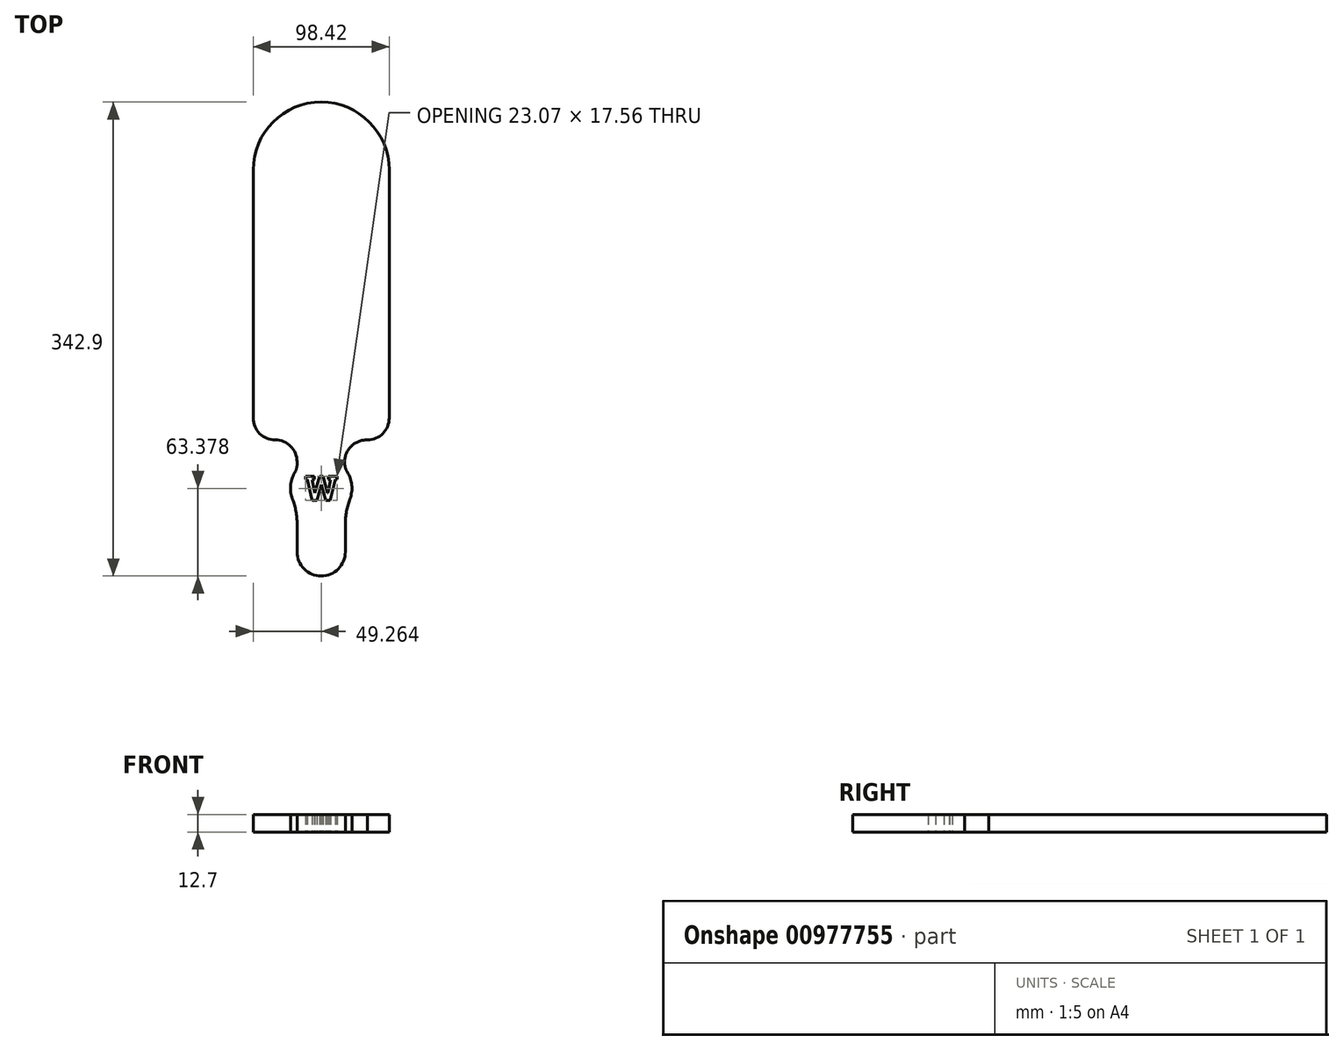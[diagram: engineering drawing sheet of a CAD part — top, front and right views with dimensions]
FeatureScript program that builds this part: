
annotation { "Feature Type Name" : "Feature", "Feature Type Description" : "" }
export const myFeature = defineFeature(function(context is Context, id is Id, definition is map)
    precondition{}
    {
        {
            var Q0;
            Q0=qCreatedBy(makeId("Top.planeOp"),FACE);
            var sketch = newSketch(context, id + "F0", { "sketchPlane" : qUnion([Q0])});
            skLineSegment(sketch, "E0.top", {"start": v(44.45, 0) * mm, "end": v(44.45, 0) * mm});
            skLineSegment(sketch, "E0.left", {"start": v(0, 298.45) * mm, "end": v(0, 117.48) * mm});
            skLineSegment(sketch, "E0.right", {"start": v(88.9, 298.45) * mm, "end": v(88.9, 117.48) * mm});
            skLineSegment(sketch, "E1.top", {"start": v(15.88, 101.6) * mm, "end": v(15.88, 101.6) * mm});
            skLineSegment(sketch, "E1.right", {"start": v(31.75, 12.7) * mm, "end": v(31.75, 85.73) * mm});
            skLineSegment(sketch, "E2.top", {"start": v(73.02, 101.6) * mm, "end": v(73.02, 101.6) * mm});
            skLineSegment(sketch, "E2.right", {"start": v(57.15, 12.7) * mm, "end": v(57.15, 85.73) * mm});
            skPoint(sketch, "E2.bottom.start.orphan", {"position": v(88.9, 0) * mm});
            skPoint(sketch, "E3.visualSharp", {"position": v(0, 101.6) * mm});
            skArc(sketch, "E3.filletArc", {"start": v(0, 117.48) * mm, "mid": v(4.65, 106.25) * mm, "end": v(15.88, 101.6) * mm});
            skPoint(sketch, "E4.visualSharp", {"position": v(88.9, 101.6) * mm});
            skArc(sketch, "E4.filletArc", {"start": v(73.02, 101.6) * mm, "mid": v(84.25, 106.25) * mm, "end": v(88.9, 117.48) * mm});
            skPoint(sketch, "E5.visualSharp", {"position": v(57.15, 101.6) * mm});
            skArc(sketch, "E5.filletArc", {"start": v(73.02, 101.6) * mm, "mid": v(61.8, 96.95) * mm, "end": v(57.15, 85.73) * mm});
            skPoint(sketch, "E6.visualSharp", {"position": v(31.75, 101.6) * mm});
            skArc(sketch, "E6.filletArc", {"start": v(31.75, 85.73) * mm, "mid": v(27.1, 96.95) * mm, "end": v(15.88, 101.6) * mm});
            skPoint(sketch, "E7.visualSharp", {"position": v(31.75, 0) * mm});
            skArc(sketch, "E7.filletArc", {"start": v(31.75, 12.7) * mm, "mid": v(35.47, 3.72) * mm, "end": v(44.45, 0) * mm});
            skPoint(sketch, "E8.visualSharp", {"position": v(57.15, 0) * mm});
            skArc(sketch, "E8.filletArc", {"start": v(44.45, 0) * mm, "mid": v(53.43, 3.72) * mm, "end": v(57.15, 12.7) * mm});
            skFitSpline(sketch, "E9", {"points": [v(31.75, 85.73) * mm, v(25.4, 50.8) * mm, v(31.75, 12.7) * mm], "startDerivative": vector(0, -58.38) * mm, "endDerivative": vector(0, -74.62) * mm});
            skFitSpline(sketch, "E10", {"points": [v(57.15, 85.73) * mm, v(63.5, 50.8) * mm, v(57.15, 12.7) * mm], "startDerivative": vector(0, -58.38) * mm, "endDerivative": vector(0, -74.62) * mm});
            skArc(sketch, "E11", {"start": v(88.9, 298.45) * mm, "mid": v(44.45, 342.9) * mm, "end": v(0, 298.45) * mm});
            skLineSegment(sketch, "E12.bottom", {"start": v(15.87, 317.5) * mm, "end": v(73.02, 317.5) * mm, "construction": true});
            skLineSegment(sketch, "E12.top", {"start": v(15.88, 117.48) * mm, "end": v(73.02, 117.48) * mm, "construction": true});
            skLineSegment(sketch, "E12.left", {"start": v(15.87, 317.5) * mm, "end": v(15.88, 117.48) * mm, "construction": true});
            skLineSegment(sketch, "E12.right", {"start": v(73.02, 317.5) * mm, "end": v(73.02, 117.48) * mm, "construction": true});
            skPoint(sketch, "E13.1.0.0", {"position": v(187.32, 0) * mm});
            skPoint(sketch, "E13.1.0.1", {"position": v(155.58, 101.6) * mm});
            skArc(sketch, "E13.1.0.2", {"start": v(187.33, 298.45) * mm, "mid": v(142.88, 342.9) * mm, "end": v(98.42, 298.45) * mm});
            skPoint(sketch, "E13.1.0.3", {"position": v(130.18, 0) * mm});
            skLineSegment(sketch, "E13.1.0.4", {"start": v(130.18, 12.7) * mm, "end": v(130.18, 85.73) * mm});
            skLineSegment(sketch, "E13.1.0.5", {"start": v(171.45, 317.5) * mm, "end": v(171.45, 117.47) * mm, "construction": true});
            skPoint(sketch, "E13.1.0.6", {"position": v(187.32, 101.6) * mm});
            skLineSegment(sketch, "E13.1.0.7", {"start": v(114.3, 317.5) * mm, "end": v(114.3, 117.47) * mm, "construction": true});
            skLineSegment(sketch, "E13.1.0.8", {"start": v(98.43, 298.45) * mm, "end": v(98.43, 117.47) * mm});
            skPoint(sketch, "E13.1.0.9", {"position": v(130.17, 101.6) * mm});
            skPoint(sketch, "E13.1.0.10", {"position": v(155.58, 0) * mm});
            skLineSegment(sketch, "E13.1.0.11", {"start": v(114.3, 317.5) * mm, "end": v(171.45, 317.5) * mm, "construction": true});
            skPoint(sketch, "E13.1.0.12", {"position": v(98.43, 101.6) * mm});
            skLineSegment(sketch, "E13.1.0.13", {"start": v(187.32, 298.45) * mm, "end": v(187.32, 117.47) * mm});
            skLineSegment(sketch, "E13.1.0.14", {"start": v(155.58, 12.7) * mm, "end": v(155.58, 85.73) * mm});
            skLineSegment(sketch, "E13.1.0.15", {"start": v(114.3, 117.47) * mm, "end": v(171.45, 117.47) * mm, "construction": true});
            skArc(sketch, "E13.1.0.16", {"start": v(98.43, 117.47) * mm, "mid": v(103.07, 106.25) * mm, "end": v(114.3, 101.6) * mm});
            skArc(sketch, "E13.1.0.17", {"start": v(171.45, 101.6) * mm, "mid": v(160.22, 96.95) * mm, "end": v(155.57, 85.73) * mm});
            skArc(sketch, "E13.1.0.18", {"start": v(130.18, 85.73) * mm, "mid": v(125.53, 96.95) * mm, "end": v(114.3, 101.6) * mm});
            skArc(sketch, "E13.1.0.19", {"start": v(142.88, 0) * mm, "mid": v(151.86, 3.72) * mm, "end": v(155.57, 12.7) * mm});
            skArc(sketch, "E13.1.0.20", {"start": v(171.45, 101.6) * mm, "mid": v(182.68, 106.25) * mm, "end": v(187.32, 117.47) * mm});
            skArc(sketch, "E13.1.0.21", {"start": v(130.17, 12.7) * mm, "mid": v(133.9, 3.72) * mm, "end": v(142.87, 0) * mm});
            skPoint(sketch, "E13.2.0.0", {"position": v(285.75, 0) * mm});
            skPoint(sketch, "E13.2.0.1", {"position": v(254, 101.6) * mm});
            skArc(sketch, "E13.2.0.2", {"start": v(285.75, 298.45) * mm, "mid": v(241.3, 342.9) * mm, "end": v(196.85, 298.45) * mm});
            skPoint(sketch, "E13.2.0.3", {"position": v(228.6, 0) * mm});
            skLineSegment(sketch, "E13.2.0.4", {"start": v(228.6, 12.7) * mm, "end": v(228.6, 85.73) * mm});
            skLineSegment(sketch, "E13.2.0.5", {"start": v(269.87, 317.5) * mm, "end": v(269.87, 117.47) * mm, "construction": true});
            skPoint(sketch, "E13.2.0.6", {"position": v(285.75, 101.6) * mm});
            skLineSegment(sketch, "E13.2.0.7", {"start": v(212.73, 317.5) * mm, "end": v(212.73, 117.47) * mm, "construction": true});
            skLineSegment(sketch, "E13.2.0.8", {"start": v(196.85, 298.45) * mm, "end": v(196.85, 117.47) * mm});
            skPoint(sketch, "E13.2.0.9", {"position": v(228.6, 101.6) * mm});
            skPoint(sketch, "E13.2.0.10", {"position": v(254, 0) * mm});
            skLineSegment(sketch, "E13.2.0.11", {"start": v(212.72, 317.5) * mm, "end": v(269.87, 317.5) * mm, "construction": true});
            skPoint(sketch, "E13.2.0.12", {"position": v(196.85, 101.6) * mm});
            skLineSegment(sketch, "E13.2.0.13", {"start": v(285.75, 298.45) * mm, "end": v(285.75, 117.47) * mm});
            skLineSegment(sketch, "E13.2.0.14", {"start": v(254, 12.7) * mm, "end": v(254, 85.73) * mm});
            skLineSegment(sketch, "E13.2.0.15", {"start": v(212.73, 117.47) * mm, "end": v(269.87, 117.47) * mm, "construction": true});
            skArc(sketch, "E13.2.0.16", {"start": v(196.85, 117.47) * mm, "mid": v(201.5, 106.25) * mm, "end": v(212.73, 101.6) * mm});
            skArc(sketch, "E13.2.0.17", {"start": v(269.88, 101.6) * mm, "mid": v(258.65, 96.95) * mm, "end": v(254, 85.73) * mm});
            skArc(sketch, "E13.2.0.18", {"start": v(228.6, 85.73) * mm, "mid": v(223.95, 96.95) * mm, "end": v(212.73, 101.6) * mm});
            skArc(sketch, "E13.2.0.19", {"start": v(241.3, 0) * mm, "mid": v(250.28, 3.72) * mm, "end": v(254, 12.7) * mm});
            skArc(sketch, "E13.2.0.20", {"start": v(269.87, 101.6) * mm, "mid": v(281.1, 106.25) * mm, "end": v(285.75, 117.47) * mm});
            skArc(sketch, "E13.2.0.21", {"start": v(228.6, 12.7) * mm, "mid": v(232.32, 3.72) * mm, "end": v(241.3, 0) * mm});
            skPoint(sketch, "E13.3.0.0", {"position": v(384.17, 0) * mm});
            skPoint(sketch, "E13.3.0.1", {"position": v(352.43, 101.6) * mm});
            skArc(sketch, "E13.3.0.2", {"start": v(384.18, 298.45) * mm, "mid": v(339.73, 342.9) * mm, "end": v(295.28, 298.45) * mm});
            skPoint(sketch, "E13.3.0.3", {"position": v(327.03, 0) * mm});
            skLineSegment(sketch, "E13.3.0.4", {"start": v(327.03, 12.7) * mm, "end": v(327.03, 85.73) * mm});
            skLineSegment(sketch, "E13.3.0.5", {"start": v(368.3, 317.5) * mm, "end": v(368.3, 117.47) * mm, "construction": true});
            skPoint(sketch, "E13.3.0.6", {"position": v(384.17, 101.6) * mm});
            skLineSegment(sketch, "E13.3.0.7", {"start": v(311.15, 317.5) * mm, "end": v(311.15, 117.47) * mm, "construction": true});
            skLineSegment(sketch, "E13.3.0.8", {"start": v(295.28, 298.45) * mm, "end": v(295.28, 117.47) * mm});
            skPoint(sketch, "E13.3.0.9", {"position": v(327.03, 101.6) * mm});
            skPoint(sketch, "E13.3.0.10", {"position": v(352.43, 0) * mm});
            skLineSegment(sketch, "E13.3.0.11", {"start": v(311.15, 317.5) * mm, "end": v(368.3, 317.5) * mm, "construction": true});
            skPoint(sketch, "E13.3.0.12", {"position": v(295.28, 101.6) * mm});
            skLineSegment(sketch, "E13.3.0.13", {"start": v(384.17, 298.45) * mm, "end": v(384.17, 117.47) * mm});
            skLineSegment(sketch, "E13.3.0.14", {"start": v(352.43, 12.7) * mm, "end": v(352.43, 85.73) * mm});
            skLineSegment(sketch, "E13.3.0.15", {"start": v(311.15, 117.47) * mm, "end": v(368.3, 117.47) * mm, "construction": true});
            skArc(sketch, "E13.3.0.16", {"start": v(295.28, 117.47) * mm, "mid": v(299.92, 106.25) * mm, "end": v(311.15, 101.6) * mm});
            skArc(sketch, "E13.3.0.17", {"start": v(368.3, 101.6) * mm, "mid": v(357.07, 96.95) * mm, "end": v(352.43, 85.73) * mm});
            skArc(sketch, "E13.3.0.18", {"start": v(327.03, 85.73) * mm, "mid": v(322.38, 96.95) * mm, "end": v(311.15, 101.6) * mm});
            skArc(sketch, "E13.3.0.19", {"start": v(339.73, 0) * mm, "mid": v(348.7, 3.72) * mm, "end": v(352.43, 12.7) * mm});
            skArc(sketch, "E13.3.0.20", {"start": v(368.3, 101.6) * mm, "mid": v(379.53, 106.25) * mm, "end": v(384.17, 117.47) * mm});
            skArc(sketch, "E13.3.0.21", {"start": v(327.02, 12.7) * mm, "mid": v(330.74, 3.72) * mm, "end": v(339.72, 0) * mm});
            skPoint(sketch, "E13.4.0.0", {"position": v(482.6, 0) * mm});
            skPoint(sketch, "E13.4.0.1", {"position": v(450.85, 101.6) * mm});
            skArc(sketch, "E13.4.0.2", {"start": v(482.6, 298.45) * mm, "mid": v(438.15, 342.9) * mm, "end": v(393.7, 298.45) * mm});
            skPoint(sketch, "E13.4.0.3", {"position": v(425.45, 0) * mm});
            skLineSegment(sketch, "E13.4.0.4", {"start": v(425.45, 12.7) * mm, "end": v(425.45, 85.73) * mm});
            skLineSegment(sketch, "E13.4.0.5", {"start": v(466.72, 317.5) * mm, "end": v(466.72, 117.47) * mm, "construction": true});
            skPoint(sketch, "E13.4.0.6", {"position": v(482.6, 101.6) * mm});
            skLineSegment(sketch, "E13.4.0.7", {"start": v(409.58, 317.5) * mm, "end": v(409.58, 117.47) * mm, "construction": true});
            skLineSegment(sketch, "E13.4.0.8", {"start": v(393.7, 298.45) * mm, "end": v(393.7, 117.47) * mm});
            skPoint(sketch, "E13.4.0.9", {"position": v(425.45, 101.6) * mm});
            skPoint(sketch, "E13.4.0.10", {"position": v(450.85, 0) * mm});
            skLineSegment(sketch, "E13.4.0.11", {"start": v(409.58, 317.5) * mm, "end": v(466.72, 317.5) * mm, "construction": true});
            skPoint(sketch, "E13.4.0.12", {"position": v(393.7, 101.6) * mm});
            skLineSegment(sketch, "E13.4.0.13", {"start": v(482.6, 298.45) * mm, "end": v(482.6, 117.47) * mm});
            skLineSegment(sketch, "E13.4.0.14", {"start": v(450.85, 12.7) * mm, "end": v(450.85, 85.73) * mm});
            skLineSegment(sketch, "E13.4.0.15", {"start": v(409.58, 117.47) * mm, "end": v(466.72, 117.47) * mm, "construction": true});
            skArc(sketch, "E13.4.0.16", {"start": v(393.7, 117.47) * mm, "mid": v(398.35, 106.25) * mm, "end": v(409.58, 101.6) * mm});
            skArc(sketch, "E13.4.0.17", {"start": v(466.73, 101.6) * mm, "mid": v(455.5, 96.95) * mm, "end": v(450.85, 85.73) * mm});
            skArc(sketch, "E13.4.0.18", {"start": v(425.45, 85.73) * mm, "mid": v(420.8, 96.95) * mm, "end": v(409.58, 101.6) * mm});
            skArc(sketch, "E13.4.0.19", {"start": v(438.15, 0) * mm, "mid": v(447.13, 3.72) * mm, "end": v(450.85, 12.7) * mm});
            skArc(sketch, "E13.4.0.20", {"start": v(466.72, 101.6) * mm, "mid": v(477.95, 106.25) * mm, "end": v(482.6, 117.47) * mm});
            skArc(sketch, "E13.4.0.21", {"start": v(425.45, 12.7) * mm, "mid": v(429.17, 3.72) * mm, "end": v(438.15, 0) * mm});
            skPoint(sketch, "E13.5.0.0", {"position": v(581.02, 0) * mm});
            skPoint(sketch, "E13.5.0.1", {"position": v(549.28, 101.6) * mm});
            skArc(sketch, "E13.5.0.2", {"start": v(581.02, 298.45) * mm, "mid": v(536.58, 342.9) * mm, "end": v(492.13, 298.45) * mm});
            skPoint(sketch, "E13.5.0.3", {"position": v(523.88, 0) * mm});
            skLineSegment(sketch, "E13.5.0.4", {"start": v(523.88, 12.7) * mm, "end": v(523.88, 85.73) * mm});
            skLineSegment(sketch, "E13.5.0.5", {"start": v(565.15, 317.5) * mm, "end": v(565.15, 117.47) * mm, "construction": true});
            skPoint(sketch, "E13.5.0.6", {"position": v(581.02, 101.6) * mm});
            skLineSegment(sketch, "E13.5.0.7", {"start": v(508, 317.5) * mm, "end": v(508, 117.47) * mm, "construction": true});
            skLineSegment(sketch, "E13.5.0.8", {"start": v(492.13, 298.45) * mm, "end": v(492.13, 117.47) * mm});
            skPoint(sketch, "E13.5.0.9", {"position": v(523.88, 101.6) * mm});
            skPoint(sketch, "E13.5.0.10", {"position": v(549.28, 0) * mm});
            skLineSegment(sketch, "E13.5.0.11", {"start": v(508, 317.5) * mm, "end": v(565.15, 317.5) * mm, "construction": true});
            skPoint(sketch, "E13.5.0.12", {"position": v(492.13, 101.6) * mm});
            skLineSegment(sketch, "E13.5.0.13", {"start": v(581.02, 298.45) * mm, "end": v(581.02, 117.47) * mm});
            skLineSegment(sketch, "E13.5.0.14", {"start": v(549.27, 12.7) * mm, "end": v(549.27, 85.73) * mm});
            skLineSegment(sketch, "E13.5.0.15", {"start": v(508, 117.47) * mm, "end": v(565.15, 117.47) * mm, "construction": true});
            skArc(sketch, "E13.5.0.16", {"start": v(492.13, 117.47) * mm, "mid": v(496.77, 106.25) * mm, "end": v(508, 101.6) * mm});
            skArc(sketch, "E13.5.0.17", {"start": v(565.15, 101.6) * mm, "mid": v(553.92, 96.95) * mm, "end": v(549.28, 85.73) * mm});
            skArc(sketch, "E13.5.0.18", {"start": v(523.88, 85.73) * mm, "mid": v(519.23, 96.95) * mm, "end": v(508, 101.6) * mm});
            skArc(sketch, "E13.5.0.19", {"start": v(536.58, 0) * mm, "mid": v(545.56, 3.72) * mm, "end": v(549.28, 12.7) * mm});
            skArc(sketch, "E13.5.0.20", {"start": v(565.15, 101.6) * mm, "mid": v(576.38, 106.25) * mm, "end": v(581.02, 117.47) * mm});
            skArc(sketch, "E13.5.0.21", {"start": v(523.87, 12.7) * mm, "mid": v(527.6, 3.72) * mm, "end": v(536.57, 0) * mm});
            skPoint(sketch, "E13.6.0.0", {"position": v(679.45, 0) * mm});
            skPoint(sketch, "E13.6.0.1", {"position": v(647.7, 101.6) * mm});
            skArc(sketch, "E13.6.0.2", {"start": v(679.45, 298.45) * mm, "mid": v(635, 342.9) * mm, "end": v(590.55, 298.45) * mm});
            skPoint(sketch, "E13.6.0.3", {"position": v(622.3, 0) * mm});
            skLineSegment(sketch, "E13.6.0.4", {"start": v(622.3, 12.7) * mm, "end": v(622.3, 85.73) * mm});
            skLineSegment(sketch, "E13.6.0.5", {"start": v(663.57, 317.5) * mm, "end": v(663.57, 117.47) * mm, "construction": true});
            skPoint(sketch, "E13.6.0.6", {"position": v(679.45, 101.6) * mm});
            skLineSegment(sketch, "E13.6.0.7", {"start": v(606.43, 317.5) * mm, "end": v(606.43, 117.47) * mm, "construction": true});
            skLineSegment(sketch, "E13.6.0.8", {"start": v(590.55, 298.45) * mm, "end": v(590.55, 117.47) * mm});
            skPoint(sketch, "E13.6.0.9", {"position": v(622.3, 101.6) * mm});
            skPoint(sketch, "E13.6.0.10", {"position": v(647.7, 0) * mm});
            skLineSegment(sketch, "E13.6.0.11", {"start": v(606.43, 317.5) * mm, "end": v(663.57, 317.5) * mm, "construction": true});
            skPoint(sketch, "E13.6.0.12", {"position": v(590.55, 101.6) * mm});
            skLineSegment(sketch, "E13.6.0.13", {"start": v(679.45, 298.45) * mm, "end": v(679.45, 117.47) * mm});
            skLineSegment(sketch, "E13.6.0.14", {"start": v(647.7, 12.7) * mm, "end": v(647.7, 85.73) * mm});
            skLineSegment(sketch, "E13.6.0.15", {"start": v(606.43, 117.47) * mm, "end": v(663.57, 117.47) * mm, "construction": true});
            skArc(sketch, "E13.6.0.16", {"start": v(590.55, 117.47) * mm, "mid": v(595.2, 106.25) * mm, "end": v(606.43, 101.6) * mm});
            skArc(sketch, "E13.6.0.17", {"start": v(663.58, 101.6) * mm, "mid": v(652.35, 96.95) * mm, "end": v(647.7, 85.73) * mm});
            skArc(sketch, "E13.6.0.18", {"start": v(622.3, 85.73) * mm, "mid": v(617.65, 96.95) * mm, "end": v(606.43, 101.6) * mm});
            skArc(sketch, "E13.6.0.19", {"start": v(635, 0) * mm, "mid": v(643.98, 3.72) * mm, "end": v(647.7, 12.7) * mm});
            skArc(sketch, "E13.6.0.20", {"start": v(663.57, 101.6) * mm, "mid": v(674.8, 106.25) * mm, "end": v(679.45, 117.47) * mm});
            skArc(sketch, "E13.6.0.21", {"start": v(622.3, 12.7) * mm, "mid": v(626.02, 3.72) * mm, "end": v(635, 0) * mm});
            skPoint(sketch, "E13.7.0.0", {"position": v(777.87, 0) * mm});
            skPoint(sketch, "E13.7.0.1", {"position": v(746.13, 101.6) * mm});
            skArc(sketch, "E13.7.0.2", {"start": v(777.88, 298.45) * mm, "mid": v(733.43, 342.9) * mm, "end": v(688.98, 298.45) * mm});
            skPoint(sketch, "E13.7.0.3", {"position": v(720.73, 0) * mm});
            skLineSegment(sketch, "E13.7.0.4", {"start": v(720.73, 12.7) * mm, "end": v(720.73, 85.73) * mm});
            skLineSegment(sketch, "E13.7.0.5", {"start": v(762, 317.5) * mm, "end": v(762, 117.47) * mm, "construction": true});
            skPoint(sketch, "E13.7.0.6", {"position": v(777.87, 101.6) * mm});
            skLineSegment(sketch, "E13.7.0.7", {"start": v(704.85, 317.5) * mm, "end": v(704.85, 117.47) * mm, "construction": true});
            skLineSegment(sketch, "E13.7.0.8", {"start": v(688.98, 298.45) * mm, "end": v(688.98, 117.47) * mm});
            skPoint(sketch, "E13.7.0.9", {"position": v(720.73, 101.6) * mm});
            skPoint(sketch, "E13.7.0.10", {"position": v(746.13, 0) * mm});
            skLineSegment(sketch, "E13.7.0.11", {"start": v(704.85, 317.5) * mm, "end": v(762, 317.5) * mm, "construction": true});
            skPoint(sketch, "E13.7.0.12", {"position": v(688.98, 101.6) * mm});
            skLineSegment(sketch, "E13.7.0.13", {"start": v(777.87, 298.45) * mm, "end": v(777.87, 117.47) * mm});
            skLineSegment(sketch, "E13.7.0.14", {"start": v(746.13, 12.7) * mm, "end": v(746.13, 85.73) * mm});
            skLineSegment(sketch, "E13.7.0.15", {"start": v(704.85, 117.47) * mm, "end": v(762, 117.47) * mm, "construction": true});
            skArc(sketch, "E13.7.0.16", {"start": v(688.98, 117.47) * mm, "mid": v(693.62, 106.25) * mm, "end": v(704.85, 101.6) * mm});
            skArc(sketch, "E13.7.0.17", {"start": v(762, 101.6) * mm, "mid": v(750.77, 96.95) * mm, "end": v(746.13, 85.73) * mm});
            skArc(sketch, "E13.7.0.18", {"start": v(720.73, 85.73) * mm, "mid": v(716.08, 96.95) * mm, "end": v(704.85, 101.6) * mm});
            skArc(sketch, "E13.7.0.19", {"start": v(733.43, 0) * mm, "mid": v(742.4, 3.72) * mm, "end": v(746.13, 12.7) * mm});
            skArc(sketch, "E13.7.0.20", {"start": v(762, 101.6) * mm, "mid": v(773.23, 106.25) * mm, "end": v(777.87, 117.47) * mm});
            skArc(sketch, "E13.7.0.21", {"start": v(720.72, 12.7) * mm, "mid": v(724.44, 3.72) * mm, "end": v(733.42, 0) * mm});
            skPoint(sketch, "E13.8.0.0", {"position": v(876.3, 0) * mm});
            skPoint(sketch, "E13.8.0.1", {"position": v(844.55, 101.6) * mm});
            skArc(sketch, "E13.8.0.2", {"start": v(876.3, 298.45) * mm, "mid": v(831.85, 342.9) * mm, "end": v(787.4, 298.45) * mm});
            skPoint(sketch, "E13.8.0.3", {"position": v(819.15, 0) * mm});
            skLineSegment(sketch, "E13.8.0.4", {"start": v(819.15, 12.7) * mm, "end": v(819.15, 85.73) * mm});
            skLineSegment(sketch, "E13.8.0.5", {"start": v(860.42, 317.5) * mm, "end": v(860.42, 117.47) * mm, "construction": true});
            skPoint(sketch, "E13.8.0.6", {"position": v(876.3, 101.6) * mm});
            skLineSegment(sketch, "E13.8.0.7", {"start": v(803.28, 317.5) * mm, "end": v(803.28, 117.47) * mm, "construction": true});
            skLineSegment(sketch, "E13.8.0.8", {"start": v(787.4, 298.45) * mm, "end": v(787.4, 117.47) * mm});
            skPoint(sketch, "E13.8.0.9", {"position": v(819.15, 101.6) * mm});
            skPoint(sketch, "E13.8.0.10", {"position": v(844.55, 0) * mm});
            skLineSegment(sketch, "E13.8.0.11", {"start": v(803.28, 317.5) * mm, "end": v(860.42, 317.5) * mm, "construction": true});
            skPoint(sketch, "E13.8.0.12", {"position": v(787.4, 101.6) * mm});
            skLineSegment(sketch, "E13.8.0.13", {"start": v(876.3, 298.45) * mm, "end": v(876.3, 117.47) * mm});
            skLineSegment(sketch, "E13.8.0.14", {"start": v(844.55, 12.7) * mm, "end": v(844.55, 85.73) * mm});
            skLineSegment(sketch, "E13.8.0.15", {"start": v(803.28, 117.47) * mm, "end": v(860.42, 117.47) * mm, "construction": true});
            skArc(sketch, "E13.8.0.16", {"start": v(787.4, 117.47) * mm, "mid": v(792.05, 106.25) * mm, "end": v(803.28, 101.6) * mm});
            skArc(sketch, "E13.8.0.17", {"start": v(860.43, 101.6) * mm, "mid": v(849.2, 96.95) * mm, "end": v(844.55, 85.73) * mm});
            skArc(sketch, "E13.8.0.18", {"start": v(819.15, 85.73) * mm, "mid": v(814.5, 96.95) * mm, "end": v(803.28, 101.6) * mm});
            skArc(sketch, "E13.8.0.19", {"start": v(831.85, 0) * mm, "mid": v(840.83, 3.72) * mm, "end": v(844.55, 12.7) * mm});
            skArc(sketch, "E13.8.0.20", {"start": v(860.42, 101.6) * mm, "mid": v(871.65, 106.25) * mm, "end": v(876.3, 117.47) * mm});
            skArc(sketch, "E13.8.0.21", {"start": v(819.15, 12.7) * mm, "mid": v(822.87, 3.72) * mm, "end": v(831.85, 0) * mm});
            skPoint(sketch, "E13.9.0.0", {"position": v(974.72, 0) * mm});
            skPoint(sketch, "E13.9.0.1", {"position": v(942.98, 101.6) * mm});
            skArc(sketch, "E13.9.0.2", {"start": v(974.73, 298.45) * mm, "mid": v(930.28, 342.9) * mm, "end": v(885.83, 298.45) * mm});
            skPoint(sketch, "E13.9.0.3", {"position": v(917.58, 0) * mm});
            skLineSegment(sketch, "E13.9.0.4", {"start": v(917.58, 12.7) * mm, "end": v(917.58, 85.73) * mm});
            skLineSegment(sketch, "E13.9.0.5", {"start": v(958.85, 317.5) * mm, "end": v(958.85, 117.47) * mm, "construction": true});
            skPoint(sketch, "E13.9.0.6", {"position": v(974.72, 101.6) * mm});
            skLineSegment(sketch, "E13.9.0.7", {"start": v(901.7, 317.5) * mm, "end": v(901.7, 117.47) * mm, "construction": true});
            skLineSegment(sketch, "E13.9.0.8", {"start": v(885.83, 298.45) * mm, "end": v(885.83, 117.47) * mm});
            skPoint(sketch, "E13.9.0.9", {"position": v(917.58, 101.6) * mm});
            skPoint(sketch, "E13.9.0.10", {"position": v(942.98, 0) * mm});
            skLineSegment(sketch, "E13.9.0.11", {"start": v(901.7, 317.5) * mm, "end": v(958.85, 317.5) * mm, "construction": true});
            skPoint(sketch, "E13.9.0.12", {"position": v(885.83, 101.6) * mm});
            skLineSegment(sketch, "E13.9.0.13", {"start": v(974.72, 298.45) * mm, "end": v(974.72, 117.47) * mm});
            skLineSegment(sketch, "E13.9.0.14", {"start": v(942.98, 12.7) * mm, "end": v(942.98, 85.73) * mm});
            skLineSegment(sketch, "E13.9.0.15", {"start": v(901.7, 117.47) * mm, "end": v(958.85, 117.47) * mm, "construction": true});
            skArc(sketch, "E13.9.0.16", {"start": v(885.83, 117.47) * mm, "mid": v(890.47, 106.25) * mm, "end": v(901.7, 101.6) * mm});
            skArc(sketch, "E13.9.0.17", {"start": v(958.85, 101.6) * mm, "mid": v(947.62, 96.95) * mm, "end": v(942.98, 85.73) * mm});
            skArc(sketch, "E13.9.0.18", {"start": v(917.58, 85.73) * mm, "mid": v(912.93, 96.95) * mm, "end": v(901.7, 101.6) * mm});
            skArc(sketch, "E13.9.0.19", {"start": v(930.28, 0) * mm, "mid": v(939.26, 3.72) * mm, "end": v(942.98, 12.7) * mm});
            skArc(sketch, "E13.9.0.20", {"start": v(958.85, 101.6) * mm, "mid": v(970.08, 106.25) * mm, "end": v(974.72, 117.47) * mm});
            skArc(sketch, "E13.9.0.21", {"start": v(917.57, 12.7) * mm, "mid": v(921.3, 3.72) * mm, "end": v(930.27, 0) * mm});
            skPoint(sketch, "E13.10.0.0", {"position": v(1073.15, 0) * mm});
            skPoint(sketch, "E13.10.0.1", {"position": v(1041.4, 101.6) * mm});
            skArc(sketch, "E13.10.0.2", {"start": v(1073.15, 298.45) * mm, "mid": v(1028.7, 342.9) * mm, "end": v(984.25, 298.45) * mm});
            skPoint(sketch, "E13.10.0.3", {"position": v(1016, 0) * mm});
            skLineSegment(sketch, "E13.10.0.4", {"start": v(1016, 12.7) * mm, "end": v(1016, 85.73) * mm});
            skLineSegment(sketch, "E13.10.0.5", {"start": v(1057.27, 317.5) * mm, "end": v(1057.27, 117.47) * mm, "construction": true});
            skPoint(sketch, "E13.10.0.6", {"position": v(1073.15, 101.6) * mm});
            skLineSegment(sketch, "E13.10.0.7", {"start": v(1000.13, 317.5) * mm, "end": v(1000.13, 117.47) * mm, "construction": true});
            skLineSegment(sketch, "E13.10.0.8", {"start": v(984.25, 298.45) * mm, "end": v(984.25, 117.47) * mm});
            skPoint(sketch, "E13.10.0.9", {"position": v(1016, 101.6) * mm});
            skPoint(sketch, "E13.10.0.10", {"position": v(1041.4, 0) * mm});
            skLineSegment(sketch, "E13.10.0.11", {"start": v(1000.13, 317.5) * mm, "end": v(1057.27, 317.5) * mm, "construction": true});
            skPoint(sketch, "E13.10.0.12", {"position": v(984.25, 101.6) * mm});
            skLineSegment(sketch, "E13.10.0.13", {"start": v(1073.15, 298.45) * mm, "end": v(1073.15, 117.47) * mm});
            skLineSegment(sketch, "E13.10.0.14", {"start": v(1041.4, 12.7) * mm, "end": v(1041.4, 85.73) * mm});
            skLineSegment(sketch, "E13.10.0.15", {"start": v(1000.13, 117.47) * mm, "end": v(1057.27, 117.47) * mm, "construction": true});
            skArc(sketch, "E13.10.0.16", {"start": v(984.25, 117.47) * mm, "mid": v(988.9, 106.25) * mm, "end": v(1000.13, 101.6) * mm});
            skArc(sketch, "E13.10.0.17", {"start": v(1057.27, 101.6) * mm, "mid": v(1046.05, 96.95) * mm, "end": v(1041.4, 85.73) * mm});
            skArc(sketch, "E13.10.0.18", {"start": v(1016, 85.73) * mm, "mid": v(1011.35, 96.95) * mm, "end": v(1000.13, 101.6) * mm});
            skArc(sketch, "E13.10.0.19", {"start": v(1028.7, 0) * mm, "mid": v(1037.68, 3.72) * mm, "end": v(1041.4, 12.7) * mm});
            skArc(sketch, "E13.10.0.20", {"start": v(1057.27, 101.6) * mm, "mid": v(1068.5, 106.25) * mm, "end": v(1073.15, 117.47) * mm});
            skArc(sketch, "E13.10.0.21", {"start": v(1016, 12.7) * mm, "mid": v(1019.72, 3.72) * mm, "end": v(1028.7, 0) * mm});
            skPoint(sketch, "E13.11.0.0", {"position": v(1171.57, 0) * mm});
            skPoint(sketch, "E13.11.0.1", {"position": v(1139.83, 101.6) * mm});
            skArc(sketch, "E13.11.0.2", {"start": v(1171.58, 298.45) * mm, "mid": v(1127.12, 342.9) * mm, "end": v(1082.67, 298.45) * mm});
            skPoint(sketch, "E13.11.0.3", {"position": v(1114.42, 0) * mm});
            skLineSegment(sketch, "E13.11.0.4", {"start": v(1114.42, 12.7) * mm, "end": v(1114.42, 85.73) * mm});
            skLineSegment(sketch, "E13.11.0.5", {"start": v(1155.7, 317.5) * mm, "end": v(1155.7, 117.47) * mm, "construction": true});
            skPoint(sketch, "E13.11.0.6", {"position": v(1171.57, 101.6) * mm});
            skLineSegment(sketch, "E13.11.0.7", {"start": v(1098.55, 317.5) * mm, "end": v(1098.55, 117.47) * mm, "construction": true});
            skLineSegment(sketch, "E13.11.0.8", {"start": v(1082.67, 298.45) * mm, "end": v(1082.67, 117.47) * mm});
            skPoint(sketch, "E13.11.0.9", {"position": v(1114.42, 101.6) * mm});
            skPoint(sketch, "E13.11.0.10", {"position": v(1139.83, 0) * mm});
            skLineSegment(sketch, "E13.11.0.11", {"start": v(1098.55, 317.5) * mm, "end": v(1155.7, 317.5) * mm, "construction": true});
            skPoint(sketch, "E13.11.0.12", {"position": v(1082.67, 101.6) * mm});
            skLineSegment(sketch, "E13.11.0.13", {"start": v(1171.57, 298.45) * mm, "end": v(1171.57, 117.47) * mm});
            skLineSegment(sketch, "E13.11.0.14", {"start": v(1139.83, 12.7) * mm, "end": v(1139.83, 85.73) * mm});
            skLineSegment(sketch, "E13.11.0.15", {"start": v(1098.55, 117.47) * mm, "end": v(1155.7, 117.47) * mm, "construction": true});
            skArc(sketch, "E13.11.0.16", {"start": v(1082.67, 117.47) * mm, "mid": v(1087.32, 106.25) * mm, "end": v(1098.55, 101.6) * mm});
            skArc(sketch, "E13.11.0.17", {"start": v(1155.7, 101.6) * mm, "mid": v(1144.47, 96.95) * mm, "end": v(1139.82, 85.73) * mm});
            skArc(sketch, "E13.11.0.18", {"start": v(1114.43, 85.73) * mm, "mid": v(1109.78, 96.95) * mm, "end": v(1098.55, 101.6) * mm});
            skArc(sketch, "E13.11.0.19", {"start": v(1127.13, 0) * mm, "mid": v(1136.1, 3.72) * mm, "end": v(1139.83, 12.7) * mm});
            skArc(sketch, "E13.11.0.20", {"start": v(1155.7, 101.6) * mm, "mid": v(1166.93, 106.25) * mm, "end": v(1171.57, 117.47) * mm});
            skArc(sketch, "E13.11.0.21", {"start": v(1114.42, 12.7) * mm, "mid": v(1118.14, 3.72) * mm, "end": v(1127.12, 0) * mm});
            skLineSegment(sketch, "E13.direction1", {"start": v(31.75, 0) * mm, "end": v(130.18, 0) * mm, "construction": true});
            skText(sketch, "E14", { "text": "W", "fontName": "NotoSerif-Regular.ttf"});
            const initialGuessF0  = {"E14": [0.03175, 0.04195, 1, 0, 0.01658]};
            skSetInitialGuess(sketch, initialGuessF0);
            skSolve(sketch);
        }
        {
            var Q0;
            Q0=qCreatedBy(makeId("Top.planeOp"),FACE);
            var sketch = newSketch(context, id + "F1", { "sketchPlane" : qUnion([Q0])});
            skLineSegment(sketch, "E15.left", {"start": v(-49.21, 114.3) * mm, "end": v(-49.21, 293.69) * mm});
            skLineSegment(sketch, "E16", {"start": v(0, 342.9) * mm, "end": v(0, 0) * mm, "construction": true});
            skArc(sketch, "E17", {"start": v(-17.46, 17.46) * mm, "mid": v(0, 0) * mm, "end": v(17.46, 17.46) * mm});
            skArc(sketch, "E18", {"start": v(49.21, 293.69) * mm, "mid": v(0, 342.9) * mm, "end": v(-49.21, 293.69) * mm});
            skLineSegment(sketch, "E19", {"start": v(-33.34, 98.43) * mm, "end": v(-33.34, 98.43) * mm});
            skArc(sketch, "E20.filletArc", {"start": v(33.34, 98.43) * mm, "mid": v(21.79, 93.96) * mm, "end": v(16.96, 82.56) * mm});
            skArc(sketch, "E21.filletArc", {"start": v(33.34, 98.43) * mm, "mid": v(44.56, 103.07) * mm, "end": v(49.21, 114.3) * mm});
            skArc(sketch, "E22.filletArc", {"start": v(-17.46, 82.55) * mm, "mid": v(-22.11, 93.78) * mm, "end": v(-33.34, 98.43) * mm});
            skArc(sketch, "E23.filletArc", {"start": v(-49.21, 114.3) * mm, "mid": v(-44.56, 103.07) * mm, "end": v(-33.34, 98.43) * mm});
            skLineSegment(sketch, "E24", {"start": v(-22.22, 63.5) * mm, "end": v(22.23, 63.5) * mm, "construction": true});
            skLineSegment(sketch, "E25.bottom", {"start": v(-31.75, 311.15) * mm, "end": v(31.75, 311.15) * mm, "construction": true});
            skLineSegment(sketch, "E25.top", {"start": v(-31.75, 114.3) * mm, "end": v(31.75, 114.3) * mm, "construction": true});
            skLineSegment(sketch, "E25.left", {"start": v(-31.75, 311.15) * mm, "end": v(-31.75, 114.3) * mm, "construction": true});
            skLineSegment(sketch, "E25.right", {"start": v(31.75, 311.15) * mm, "end": v(31.75, 114.3) * mm, "construction": true});
            skArc(sketch, "E26", {"start": v(-19.2, 74.7) * mm, "mid": v(-22.15, 65.33) * mm, "end": v(-20.78, 55.6) * mm});
            skLineSegment(sketch, "E27", {"start": v(-17.46, 82.55) * mm, "end": v(-17.46, 81.1) * mm});
            skLineSegment(sketch, "E28.trimOffspring", {"start": v(-17.46, 37.56) * mm, "end": v(-17.46, 17.46) * mm});
            skLineSegment(sketch, "E29.trimOffspring", {"start": v(17.46, 37.56) * mm, "end": v(17.46, 17.46) * mm});
            skArc(sketch, "E30.trimOffspring", {"start": v(20.78, 55.6) * mm, "mid": v(22.12, 65.66) * mm, "end": v(18.85, 75.27) * mm});
            skPoint(sketch, "E31.visualSharp", {"position": v(-17.46, 77.25) * mm});
            skArc(sketch, "E31.filletArc", {"start": v(-19.2, 74.7) * mm, "mid": v(-17.9, 77.8) * mm, "end": v(-17.46, 81.1) * mm});
            skPoint(sketch, "E32.visualSharp", {"position": v(-17.46, 49.75) * mm});
            skArc(sketch, "E32.filletArc", {"start": v(-17.46, 37.56) * mm, "mid": v(-18.3, 46.73) * mm, "end": v(-20.78, 55.6) * mm});
            skPoint(sketch, "E33.visualSharp", {"position": v(17.46, 49.75) * mm});
            skArc(sketch, "E33.filletArc", {"start": v(20.78, 55.6) * mm, "mid": v(18.3, 46.73) * mm, "end": v(17.46, 37.56) * mm});
            skPoint(sketch, "E34.visualSharp", {"position": v(17.46, 83.6) * mm});
            skArc(sketch, "E34.filletArc", {"start": v(16.96, 81.11) * mm, "mid": v(17.55, 78.08) * mm, "end": v(18.85, 75.27) * mm});
            skText(sketch, "E35", { "text": "W", "fontName": "RobotoSlab-Bold.ttf"});
            skLineSegment(sketch, "E36", {"start": v(16.96, 81.11) * mm, "end": v(16.96, 82.56) * mm});
            skLineSegment(sketch, "E37", {"start": v(33.34, 98.43) * mm, "end": v(33.34, 98.43) * mm});
            skLineSegment(sketch, "E38.direction1", {"start": v(-68.26, 37.56) * mm, "end": v(30.16, 37.56) * mm, "construction": true});
            skLineSegment(sketch, "E39.1.0.0", {"start": v(66.68, 311.15) * mm, "end": v(130.17, 311.15) * mm, "construction": true});
            skLineSegment(sketch, "E39.1.0.1", {"start": v(130.18, 311.15) * mm, "end": v(130.17, 114.3) * mm, "construction": true});
            skLineSegment(sketch, "E39.1.0.2", {"start": v(49.21, 114.3) * mm, "end": v(49.21, 293.69) * mm});
            skArc(sketch, "E39.1.0.3", {"start": v(147.64, 293.69) * mm, "mid": v(98.42, 342.9) * mm, "end": v(49.21, 293.69) * mm});
            skLineSegment(sketch, "E39.1.0.4", {"start": v(66.67, 114.3) * mm, "end": v(130.18, 114.3) * mm, "construction": true});
            skPoint(sketch, "E39.1.0.5", {"position": v(80.96, 49.75) * mm});
            skLineSegment(sketch, "E39.1.0.6", {"start": v(66.68, 311.15) * mm, "end": v(66.67, 114.3) * mm, "construction": true});
            skLineSegment(sketch, "E39.1.0.7", {"start": v(98.42, 342.9) * mm, "end": v(98.43, 0) * mm, "construction": true});
            skPoint(sketch, "E39.1.0.8", {"position": v(115.89, 83.6) * mm});
            skArc(sketch, "E39.1.0.9", {"start": v(49.21, 114.3) * mm, "mid": v(53.86, 103.07) * mm, "end": v(65.09, 98.43) * mm});
            skArc(sketch, "E39.1.0.10", {"start": v(131.76, 98.43) * mm, "mid": v(142.99, 103.07) * mm, "end": v(147.64, 114.3) * mm});
            skLineSegment(sketch, "E39.1.0.11", {"start": v(30.16, 37.56) * mm, "end": v(128.58, 38.71) * mm, "construction": true});
            skPoint(sketch, "E39.1.0.12", {"position": v(80.96, 77.25) * mm});
            skPoint(sketch, "E39.1.0.13", {"position": v(115.89, 49.75) * mm});
            skArc(sketch, "E39.1.0.14", {"start": v(80.96, 17.46) * mm, "mid": v(98.43, 0) * mm, "end": v(115.89, 17.46) * mm});
            skArc(sketch, "E39.1.0.15", {"start": v(80.96, 82.55) * mm, "mid": v(76.31, 93.78) * mm, "end": v(65.09, 98.43) * mm});
            skLineSegment(sketch, "E39.1.0.16", {"start": v(30.16, 37.56) * mm, "end": v(128.59, 37.56) * mm, "construction": true});
            skArc(sketch, "E39.1.0.17", {"start": v(80.96, 37.56) * mm, "mid": v(80.13, 46.73) * mm, "end": v(77.65, 55.6) * mm});
            skArc(sketch, "E39.1.0.18", {"start": v(131.76, 98.43) * mm, "mid": v(120.21, 93.96) * mm, "end": v(115.38, 82.56) * mm});
            skLineSegment(sketch, "E39.1.0.19", {"start": v(115.89, 37.56) * mm, "end": v(115.89, 17.46) * mm});
            skLineSegment(sketch, "E39.1.0.20", {"start": v(76.2, 63.5) * mm, "end": v(120.65, 63.5) * mm, "construction": true});
            skArc(sketch, "E39.1.0.21", {"start": v(79.23, 74.7) * mm, "mid": v(76.28, 65.33) * mm, "end": v(77.65, 55.6) * mm});
            skLineSegment(sketch, "E39.1.0.22", {"start": v(80.96, 37.56) * mm, "end": v(80.96, 17.46) * mm});
            skArc(sketch, "E39.1.0.23", {"start": v(119.2, 55.6) * mm, "mid": v(120.54, 65.66) * mm, "end": v(117.28, 75.27) * mm});
            skArc(sketch, "E39.1.0.24", {"start": v(119.2, 55.6) * mm, "mid": v(116.72, 46.73) * mm, "end": v(115.89, 37.56) * mm});
            skLineSegment(sketch, "E39.1.0.25", {"start": v(115.38, 81.11) * mm, "end": v(115.38, 82.56) * mm});
            skArc(sketch, "E39.1.0.26", {"start": v(115.38, 81.11) * mm, "mid": v(115.97, 78.08) * mm, "end": v(117.28, 75.27) * mm});
            skLineSegment(sketch, "E39.1.0.27", {"start": v(80.96, 82.55) * mm, "end": v(80.96, 81.1) * mm});
            skArc(sketch, "E39.1.0.28", {"start": v(79.23, 74.7) * mm, "mid": v(80.52, 77.8) * mm, "end": v(80.96, 81.1) * mm});
            skLineSegment(sketch, "E39.2.0.0", {"start": v(165.1, 311.15) * mm, "end": v(228.6, 311.15) * mm, "construction": true});
            skLineSegment(sketch, "E39.2.0.1", {"start": v(228.6, 311.15) * mm, "end": v(228.6, 114.3) * mm, "construction": true});
            skLineSegment(sketch, "E39.2.0.2", {"start": v(147.64, 114.3) * mm, "end": v(147.64, 293.69) * mm});
            skArc(sketch, "E39.2.0.3", {"start": v(246.06, 293.69) * mm, "mid": v(196.85, 342.9) * mm, "end": v(147.64, 293.69) * mm});
            skLineSegment(sketch, "E39.2.0.4", {"start": v(165.1, 114.3) * mm, "end": v(228.6, 114.3) * mm, "construction": true});
            skPoint(sketch, "E39.2.0.5", {"position": v(179.39, 49.75) * mm});
            skLineSegment(sketch, "E39.2.0.6", {"start": v(165.1, 311.15) * mm, "end": v(165.1, 114.3) * mm, "construction": true});
            skLineSegment(sketch, "E39.2.0.7", {"start": v(196.85, 342.9) * mm, "end": v(196.85, 0) * mm, "construction": true});
            skPoint(sketch, "E39.2.0.8", {"position": v(214.31, 83.6) * mm});
            skArc(sketch, "E39.2.0.9", {"start": v(147.64, 114.3) * mm, "mid": v(152.29, 103.07) * mm, "end": v(163.51, 98.43) * mm});
            skArc(sketch, "E39.2.0.10", {"start": v(230.19, 98.43) * mm, "mid": v(241.41, 103.07) * mm, "end": v(246.06, 114.3) * mm});
            skLineSegment(sketch, "E39.2.0.11", {"start": v(128.59, 37.56) * mm, "end": v(227, 38.71) * mm, "construction": true});
            skPoint(sketch, "E39.2.0.12", {"position": v(179.39, 77.25) * mm});
            skPoint(sketch, "E39.2.0.13", {"position": v(214.31, 49.75) * mm});
            skArc(sketch, "E39.2.0.14", {"start": v(179.39, 17.46) * mm, "mid": v(196.85, 0) * mm, "end": v(214.31, 17.46) * mm});
            skArc(sketch, "E39.2.0.15", {"start": v(179.39, 82.55) * mm, "mid": v(174.74, 93.78) * mm, "end": v(163.51, 98.43) * mm});
            skLineSegment(sketch, "E39.2.0.16", {"start": v(128.59, 37.56) * mm, "end": v(227.01, 37.56) * mm, "construction": true});
            skArc(sketch, "E39.2.0.17", {"start": v(179.39, 37.56) * mm, "mid": v(178.55, 46.73) * mm, "end": v(176.07, 55.6) * mm});
            skArc(sketch, "E39.2.0.18", {"start": v(230.19, 98.43) * mm, "mid": v(218.64, 93.96) * mm, "end": v(213.8, 82.56) * mm});
            skLineSegment(sketch, "E39.2.0.19", {"start": v(214.31, 37.56) * mm, "end": v(214.31, 17.46) * mm});
            skLineSegment(sketch, "E39.2.0.20", {"start": v(174.63, 63.5) * mm, "end": v(219.08, 63.5) * mm, "construction": true});
            skArc(sketch, "E39.2.0.21", {"start": v(177.66, 74.7) * mm, "mid": v(174.7, 65.33) * mm, "end": v(176.07, 55.6) * mm});
            skLineSegment(sketch, "E39.2.0.22", {"start": v(179.39, 37.56) * mm, "end": v(179.39, 17.46) * mm});
            skArc(sketch, "E39.2.0.23", {"start": v(217.63, 55.6) * mm, "mid": v(218.97, 65.66) * mm, "end": v(215.7, 75.27) * mm});
            skArc(sketch, "E39.2.0.24", {"start": v(217.63, 55.6) * mm, "mid": v(215.15, 46.73) * mm, "end": v(214.31, 37.56) * mm});
            skLineSegment(sketch, "E39.2.0.25", {"start": v(213.8, 81.11) * mm, "end": v(213.8, 82.56) * mm});
            skArc(sketch, "E39.2.0.26", {"start": v(213.8, 81.11) * mm, "mid": v(214.4, 78.08) * mm, "end": v(215.7, 75.27) * mm});
            skLineSegment(sketch, "E39.2.0.27", {"start": v(179.39, 82.55) * mm, "end": v(179.39, 81.1) * mm});
            skArc(sketch, "E39.2.0.28", {"start": v(177.66, 74.7) * mm, "mid": v(178.95, 77.8) * mm, "end": v(179.39, 81.1) * mm});
            skLineSegment(sketch, "E39.3.0.0", {"start": v(263.53, 311.15) * mm, "end": v(327.03, 311.15) * mm, "construction": true});
            skLineSegment(sketch, "E39.3.0.1", {"start": v(327.03, 311.15) * mm, "end": v(327.03, 114.3) * mm, "construction": true});
            skLineSegment(sketch, "E39.3.0.2", {"start": v(246.06, 114.3) * mm, "end": v(246.06, 293.69) * mm});
            skArc(sketch, "E39.3.0.3", {"start": v(344.49, 293.69) * mm, "mid": v(295.28, 342.9) * mm, "end": v(246.06, 293.69) * mm});
            skLineSegment(sketch, "E39.3.0.4", {"start": v(263.53, 114.3) * mm, "end": v(327.03, 114.3) * mm, "construction": true});
            skPoint(sketch, "E39.3.0.5", {"position": v(277.81, 49.75) * mm});
            skLineSegment(sketch, "E39.3.0.6", {"start": v(263.53, 311.15) * mm, "end": v(263.52, 114.3) * mm, "construction": true});
            skLineSegment(sketch, "E39.3.0.7", {"start": v(295.28, 342.9) * mm, "end": v(295.28, 0) * mm, "construction": true});
            skPoint(sketch, "E39.3.0.8", {"position": v(312.74, 83.6) * mm});
            skArc(sketch, "E39.3.0.9", {"start": v(246.06, 114.3) * mm, "mid": v(250.71, 103.07) * mm, "end": v(261.94, 98.43) * mm});
            skArc(sketch, "E39.3.0.10", {"start": v(328.61, 98.43) * mm, "mid": v(339.84, 103.07) * mm, "end": v(344.49, 114.3) * mm});
            skLineSegment(sketch, "E39.3.0.11", {"start": v(227.01, 37.56) * mm, "end": v(325.43, 38.71) * mm, "construction": true});
            skPoint(sketch, "E39.3.0.12", {"position": v(277.81, 77.25) * mm});
            skPoint(sketch, "E39.3.0.13", {"position": v(312.74, 49.75) * mm});
            skArc(sketch, "E39.3.0.14", {"start": v(277.81, 17.46) * mm, "mid": v(295.28, 0) * mm, "end": v(312.74, 17.46) * mm});
            skArc(sketch, "E39.3.0.15", {"start": v(277.81, 82.55) * mm, "mid": v(273.16, 93.78) * mm, "end": v(261.94, 98.43) * mm});
            skLineSegment(sketch, "E39.3.0.16", {"start": v(227.01, 37.56) * mm, "end": v(325.44, 37.56) * mm, "construction": true});
            skArc(sketch, "E39.3.0.17", {"start": v(277.81, 37.56) * mm, "mid": v(276.98, 46.73) * mm, "end": v(274.5, 55.6) * mm});
            skArc(sketch, "E39.3.0.18", {"start": v(328.61, 98.43) * mm, "mid": v(317.06, 93.96) * mm, "end": v(312.23, 82.56) * mm});
            skLineSegment(sketch, "E39.3.0.19", {"start": v(312.74, 37.56) * mm, "end": v(312.74, 17.46) * mm});
            skLineSegment(sketch, "E39.3.0.20", {"start": v(273.05, 63.5) * mm, "end": v(317.5, 63.5) * mm, "construction": true});
            skArc(sketch, "E39.3.0.21", {"start": v(276.08, 74.7) * mm, "mid": v(273.13, 65.33) * mm, "end": v(274.5, 55.6) * mm});
            skLineSegment(sketch, "E39.3.0.22", {"start": v(277.81, 37.56) * mm, "end": v(277.81, 17.46) * mm});
            skArc(sketch, "E39.3.0.23", {"start": v(316.05, 55.6) * mm, "mid": v(317.4, 65.66) * mm, "end": v(314.13, 75.27) * mm});
            skArc(sketch, "E39.3.0.24", {"start": v(316.05, 55.6) * mm, "mid": v(313.57, 46.73) * mm, "end": v(312.74, 37.56) * mm});
            skLineSegment(sketch, "E39.3.0.25", {"start": v(312.23, 81.11) * mm, "end": v(312.23, 82.56) * mm});
            skArc(sketch, "E39.3.0.26", {"start": v(312.23, 81.11) * mm, "mid": v(312.82, 78.08) * mm, "end": v(314.13, 75.27) * mm});
            skLineSegment(sketch, "E39.3.0.27", {"start": v(277.81, 82.55) * mm, "end": v(277.81, 81.1) * mm});
            skArc(sketch, "E39.3.0.28", {"start": v(276.08, 74.7) * mm, "mid": v(277.37, 77.8) * mm, "end": v(277.81, 81.1) * mm});
            skLineSegment(sketch, "E39.4.0.0", {"start": v(361.95, 311.15) * mm, "end": v(425.45, 311.15) * mm, "construction": true});
            skLineSegment(sketch, "E39.4.0.1", {"start": v(425.45, 311.15) * mm, "end": v(425.45, 114.3) * mm, "construction": true});
            skLineSegment(sketch, "E39.4.0.2", {"start": v(344.49, 114.3) * mm, "end": v(344.49, 293.69) * mm});
            skArc(sketch, "E39.4.0.3", {"start": v(442.91, 293.69) * mm, "mid": v(393.7, 342.9) * mm, "end": v(344.49, 293.69) * mm});
            skLineSegment(sketch, "E39.4.0.4", {"start": v(361.95, 114.3) * mm, "end": v(425.45, 114.3) * mm, "construction": true});
            skPoint(sketch, "E39.4.0.5", {"position": v(376.24, 49.75) * mm});
            skLineSegment(sketch, "E39.4.0.6", {"start": v(361.95, 311.15) * mm, "end": v(361.95, 114.3) * mm, "construction": true});
            skLineSegment(sketch, "E39.4.0.7", {"start": v(393.7, 342.9) * mm, "end": v(393.7, 0) * mm, "construction": true});
            skPoint(sketch, "E39.4.0.8", {"position": v(411.16, 83.6) * mm});
            skArc(sketch, "E39.4.0.9", {"start": v(344.49, 114.3) * mm, "mid": v(349.14, 103.07) * mm, "end": v(360.36, 98.43) * mm});
            skArc(sketch, "E39.4.0.10", {"start": v(427.04, 98.43) * mm, "mid": v(438.26, 103.07) * mm, "end": v(442.91, 114.3) * mm});
            skLineSegment(sketch, "E39.4.0.11", {"start": v(325.44, 37.56) * mm, "end": v(423.86, 38.71) * mm, "construction": true});
            skPoint(sketch, "E39.4.0.12", {"position": v(376.24, 77.25) * mm});
            skPoint(sketch, "E39.4.0.13", {"position": v(411.16, 49.75) * mm});
            skArc(sketch, "E39.4.0.14", {"start": v(376.24, 17.46) * mm, "mid": v(393.7, 0) * mm, "end": v(411.16, 17.46) * mm});
            skArc(sketch, "E39.4.0.15", {"start": v(376.24, 82.55) * mm, "mid": v(371.59, 93.78) * mm, "end": v(360.36, 98.43) * mm});
            skLineSegment(sketch, "E39.4.0.16", {"start": v(325.44, 37.56) * mm, "end": v(423.86, 37.56) * mm, "construction": true});
            skArc(sketch, "E39.4.0.17", {"start": v(376.24, 37.56) * mm, "mid": v(375.4, 46.73) * mm, "end": v(372.92, 55.6) * mm});
            skArc(sketch, "E39.4.0.18", {"start": v(427.04, 98.43) * mm, "mid": v(415.49, 93.96) * mm, "end": v(410.66, 82.56) * mm});
            skLineSegment(sketch, "E39.4.0.19", {"start": v(411.16, 37.56) * mm, "end": v(411.16, 17.46) * mm});
            skLineSegment(sketch, "E39.4.0.20", {"start": v(371.48, 63.5) * mm, "end": v(415.93, 63.5) * mm, "construction": true});
            skArc(sketch, "E39.4.0.21", {"start": v(374.5, 74.7) * mm, "mid": v(371.55, 65.33) * mm, "end": v(372.92, 55.6) * mm});
            skLineSegment(sketch, "E39.4.0.22", {"start": v(376.24, 37.56) * mm, "end": v(376.24, 17.46) * mm});
            skArc(sketch, "E39.4.0.23", {"start": v(414.48, 55.6) * mm, "mid": v(415.82, 65.66) * mm, "end": v(412.55, 75.27) * mm});
            skArc(sketch, "E39.4.0.24", {"start": v(414.48, 55.6) * mm, "mid": v(412, 46.73) * mm, "end": v(411.16, 37.56) * mm});
            skLineSegment(sketch, "E39.4.0.25", {"start": v(410.66, 81.11) * mm, "end": v(410.66, 82.56) * mm});
            skArc(sketch, "E39.4.0.26", {"start": v(410.66, 81.11) * mm, "mid": v(411.25, 78.08) * mm, "end": v(412.55, 75.27) * mm});
            skLineSegment(sketch, "E39.4.0.27", {"start": v(376.24, 82.55) * mm, "end": v(376.24, 81.1) * mm});
            skArc(sketch, "E39.4.0.28", {"start": v(374.5, 74.7) * mm, "mid": v(375.8, 77.8) * mm, "end": v(376.24, 81.1) * mm});
            skLineSegment(sketch, "E39.5.0.0", {"start": v(460.38, 311.15) * mm, "end": v(523.88, 311.15) * mm, "construction": true});
            skLineSegment(sketch, "E39.5.0.1", {"start": v(523.88, 311.15) * mm, "end": v(523.87, 114.3) * mm, "construction": true});
            skLineSegment(sketch, "E39.5.0.2", {"start": v(442.91, 114.3) * mm, "end": v(442.91, 293.69) * mm});
            skArc(sketch, "E39.5.0.3", {"start": v(541.34, 293.69) * mm, "mid": v(492.13, 342.9) * mm, "end": v(442.91, 293.69) * mm});
            skLineSegment(sketch, "E39.5.0.4", {"start": v(460.38, 114.3) * mm, "end": v(523.88, 114.3) * mm, "construction": true});
            skPoint(sketch, "E39.5.0.5", {"position": v(474.66, 49.75) * mm});
            skLineSegment(sketch, "E39.5.0.6", {"start": v(460.38, 311.15) * mm, "end": v(460.37, 114.3) * mm, "construction": true});
            skLineSegment(sketch, "E39.5.0.7", {"start": v(492.12, 342.9) * mm, "end": v(492.13, 0) * mm, "construction": true});
            skPoint(sketch, "E39.5.0.8", {"position": v(509.59, 83.6) * mm});
            skArc(sketch, "E39.5.0.9", {"start": v(442.91, 114.3) * mm, "mid": v(447.56, 103.07) * mm, "end": v(458.79, 98.43) * mm});
            skArc(sketch, "E39.5.0.10", {"start": v(525.46, 98.43) * mm, "mid": v(536.69, 103.07) * mm, "end": v(541.34, 114.3) * mm});
            skLineSegment(sketch, "E39.5.0.11", {"start": v(423.86, 37.56) * mm, "end": v(522.28, 38.71) * mm, "construction": true});
            skPoint(sketch, "E39.5.0.12", {"position": v(474.66, 77.25) * mm});
            skPoint(sketch, "E39.5.0.13", {"position": v(509.59, 49.75) * mm});
            skArc(sketch, "E39.5.0.14", {"start": v(474.66, 17.46) * mm, "mid": v(492.13, 0) * mm, "end": v(509.59, 17.46) * mm});
            skArc(sketch, "E39.5.0.15", {"start": v(474.66, 82.55) * mm, "mid": v(470.01, 93.78) * mm, "end": v(458.79, 98.43) * mm});
            skLineSegment(sketch, "E39.5.0.16", {"start": v(423.86, 37.56) * mm, "end": v(522.29, 37.56) * mm, "construction": true});
            skArc(sketch, "E39.5.0.17", {"start": v(474.66, 37.56) * mm, "mid": v(473.83, 46.73) * mm, "end": v(471.35, 55.6) * mm});
            skArc(sketch, "E39.5.0.18", {"start": v(525.46, 98.43) * mm, "mid": v(513.91, 93.96) * mm, "end": v(509.08, 82.56) * mm});
            skLineSegment(sketch, "E39.5.0.19", {"start": v(509.59, 37.56) * mm, "end": v(509.59, 17.46) * mm});
            skLineSegment(sketch, "E39.5.0.20", {"start": v(469.9, 63.5) * mm, "end": v(514.35, 63.5) * mm, "construction": true});
            skArc(sketch, "E39.5.0.21", {"start": v(472.93, 74.7) * mm, "mid": v(469.98, 65.33) * mm, "end": v(471.35, 55.6) * mm});
            skLineSegment(sketch, "E39.5.0.22", {"start": v(474.66, 37.56) * mm, "end": v(474.66, 17.46) * mm});
            skArc(sketch, "E39.5.0.23", {"start": v(512.9, 55.6) * mm, "mid": v(514.24, 65.66) * mm, "end": v(510.98, 75.27) * mm});
            skArc(sketch, "E39.5.0.24", {"start": v(512.9, 55.6) * mm, "mid": v(510.42, 46.73) * mm, "end": v(509.59, 37.56) * mm});
            skLineSegment(sketch, "E39.5.0.25", {"start": v(509.08, 81.11) * mm, "end": v(509.08, 82.56) * mm});
            skArc(sketch, "E39.5.0.26", {"start": v(509.08, 81.11) * mm, "mid": v(509.67, 78.08) * mm, "end": v(510.98, 75.27) * mm});
            skLineSegment(sketch, "E39.5.0.27", {"start": v(474.66, 82.55) * mm, "end": v(474.66, 81.1) * mm});
            skArc(sketch, "E39.5.0.28", {"start": v(472.93, 74.7) * mm, "mid": v(474.22, 77.8) * mm, "end": v(474.66, 81.1) * mm});
            skLineSegment(sketch, "E39.6.0.0", {"start": v(558.8, 311.15) * mm, "end": v(622.3, 311.15) * mm, "construction": true});
            skLineSegment(sketch, "E39.6.0.1", {"start": v(622.3, 311.15) * mm, "end": v(622.3, 114.3) * mm, "construction": true});
            skLineSegment(sketch, "E39.6.0.2", {"start": v(541.34, 114.3) * mm, "end": v(541.34, 293.69) * mm});
            skArc(sketch, "E39.6.0.3", {"start": v(639.76, 293.69) * mm, "mid": v(590.55, 342.9) * mm, "end": v(541.34, 293.69) * mm});
            skLineSegment(sketch, "E39.6.0.4", {"start": v(558.8, 114.3) * mm, "end": v(622.3, 114.3) * mm, "construction": true});
            skPoint(sketch, "E39.6.0.5", {"position": v(573.09, 49.75) * mm});
            skLineSegment(sketch, "E39.6.0.6", {"start": v(558.8, 311.15) * mm, "end": v(558.8, 114.3) * mm, "construction": true});
            skLineSegment(sketch, "E39.6.0.7", {"start": v(590.55, 342.9) * mm, "end": v(590.55, 0) * mm, "construction": true});
            skPoint(sketch, "E39.6.0.8", {"position": v(608.01, 83.6) * mm});
            skArc(sketch, "E39.6.0.9", {"start": v(541.34, 114.3) * mm, "mid": v(545.99, 103.07) * mm, "end": v(557.21, 98.43) * mm});
            skArc(sketch, "E39.6.0.10", {"start": v(623.89, 98.43) * mm, "mid": v(635.11, 103.07) * mm, "end": v(639.76, 114.3) * mm});
            skLineSegment(sketch, "E39.6.0.11", {"start": v(522.29, 37.56) * mm, "end": v(620.7, 38.71) * mm, "construction": true});
            skPoint(sketch, "E39.6.0.12", {"position": v(573.09, 77.25) * mm});
            skPoint(sketch, "E39.6.0.13", {"position": v(608.01, 49.75) * mm});
            skArc(sketch, "E39.6.0.14", {"start": v(573.09, 17.46) * mm, "mid": v(590.55, 0) * mm, "end": v(608.01, 17.46) * mm});
            skArc(sketch, "E39.6.0.15", {"start": v(573.09, 82.55) * mm, "mid": v(568.44, 93.78) * mm, "end": v(557.21, 98.43) * mm});
            skLineSegment(sketch, "E39.6.0.16", {"start": v(522.29, 37.56) * mm, "end": v(620.71, 37.56) * mm, "construction": true});
            skArc(sketch, "E39.6.0.17", {"start": v(573.09, 37.56) * mm, "mid": v(572.25, 46.73) * mm, "end": v(569.77, 55.6) * mm});
            skArc(sketch, "E39.6.0.18", {"start": v(623.89, 98.43) * mm, "mid": v(612.34, 93.96) * mm, "end": v(607.5, 82.56) * mm});
            skLineSegment(sketch, "E39.6.0.19", {"start": v(608.01, 37.56) * mm, "end": v(608.01, 17.46) * mm});
            skLineSegment(sketch, "E39.6.0.20", {"start": v(568.33, 63.5) * mm, "end": v(612.78, 63.5) * mm, "construction": true});
            skArc(sketch, "E39.6.0.21", {"start": v(571.36, 74.7) * mm, "mid": v(568.4, 65.33) * mm, "end": v(569.77, 55.6) * mm});
            skLineSegment(sketch, "E39.6.0.22", {"start": v(573.09, 37.56) * mm, "end": v(573.09, 17.46) * mm});
            skArc(sketch, "E39.6.0.23", {"start": v(611.33, 55.6) * mm, "mid": v(612.67, 65.66) * mm, "end": v(609.4, 75.27) * mm});
            skArc(sketch, "E39.6.0.24", {"start": v(611.33, 55.6) * mm, "mid": v(608.85, 46.73) * mm, "end": v(608.01, 37.56) * mm});
            skLineSegment(sketch, "E39.6.0.25", {"start": v(607.5, 81.11) * mm, "end": v(607.5, 82.56) * mm});
            skArc(sketch, "E39.6.0.26", {"start": v(607.5, 81.11) * mm, "mid": v(608.1, 78.08) * mm, "end": v(609.4, 75.27) * mm});
            skLineSegment(sketch, "E39.6.0.27", {"start": v(573.09, 82.55) * mm, "end": v(573.09, 81.1) * mm});
            skArc(sketch, "E39.6.0.28", {"start": v(571.36, 74.7) * mm, "mid": v(572.65, 77.8) * mm, "end": v(573.09, 81.1) * mm});
            skLineSegment(sketch, "E39.7.0.0", {"start": v(657.23, 311.15) * mm, "end": v(720.73, 311.15) * mm, "construction": true});
            skLineSegment(sketch, "E39.7.0.1", {"start": v(720.73, 311.15) * mm, "end": v(720.73, 114.3) * mm, "construction": true});
            skLineSegment(sketch, "E39.7.0.2", {"start": v(639.76, 114.3) * mm, "end": v(639.76, 293.69) * mm});
            skArc(sketch, "E39.7.0.3", {"start": v(738.19, 293.69) * mm, "mid": v(688.98, 342.9) * mm, "end": v(639.76, 293.69) * mm});
            skLineSegment(sketch, "E39.7.0.4", {"start": v(657.23, 114.3) * mm, "end": v(720.73, 114.3) * mm, "construction": true});
            skPoint(sketch, "E39.7.0.5", {"position": v(671.51, 49.75) * mm});
            skLineSegment(sketch, "E39.7.0.6", {"start": v(657.23, 311.15) * mm, "end": v(657.23, 114.3) * mm, "construction": true});
            skLineSegment(sketch, "E39.7.0.7", {"start": v(688.98, 342.9) * mm, "end": v(688.98, 0) * mm, "construction": true});
            skPoint(sketch, "E39.7.0.8", {"position": v(706.44, 83.6) * mm});
            skArc(sketch, "E39.7.0.9", {"start": v(639.76, 114.3) * mm, "mid": v(644.41, 103.07) * mm, "end": v(655.64, 98.43) * mm});
            skArc(sketch, "E39.7.0.10", {"start": v(722.31, 98.43) * mm, "mid": v(733.54, 103.07) * mm, "end": v(738.19, 114.3) * mm});
            skLineSegment(sketch, "E39.7.0.11", {"start": v(620.71, 37.56) * mm, "end": v(719.13, 38.71) * mm, "construction": true});
            skPoint(sketch, "E39.7.0.12", {"position": v(671.51, 77.25) * mm});
            skPoint(sketch, "E39.7.0.13", {"position": v(706.44, 49.75) * mm});
            skArc(sketch, "E39.7.0.14", {"start": v(671.51, 17.46) * mm, "mid": v(688.98, 0) * mm, "end": v(706.44, 17.46) * mm});
            skArc(sketch, "E39.7.0.15", {"start": v(671.51, 82.55) * mm, "mid": v(666.86, 93.78) * mm, "end": v(655.64, 98.43) * mm});
            skLineSegment(sketch, "E39.7.0.16", {"start": v(620.71, 37.56) * mm, "end": v(719.14, 37.56) * mm, "construction": true});
            skArc(sketch, "E39.7.0.17", {"start": v(671.51, 37.56) * mm, "mid": v(670.68, 46.73) * mm, "end": v(668.2, 55.6) * mm});
            skArc(sketch, "E39.7.0.18", {"start": v(722.31, 98.43) * mm, "mid": v(710.76, 93.96) * mm, "end": v(705.93, 82.56) * mm});
            skLineSegment(sketch, "E39.7.0.19", {"start": v(706.44, 37.56) * mm, "end": v(706.44, 17.46) * mm});
            skLineSegment(sketch, "E39.7.0.20", {"start": v(666.75, 63.5) * mm, "end": v(711.2, 63.5) * mm, "construction": true});
            skArc(sketch, "E39.7.0.21", {"start": v(669.78, 74.7) * mm, "mid": v(666.83, 65.33) * mm, "end": v(668.2, 55.6) * mm});
            skLineSegment(sketch, "E39.7.0.22", {"start": v(671.51, 37.56) * mm, "end": v(671.51, 17.46) * mm});
            skArc(sketch, "E39.7.0.23", {"start": v(709.75, 55.6) * mm, "mid": v(711.1, 65.66) * mm, "end": v(707.83, 75.27) * mm});
            skArc(sketch, "E39.7.0.24", {"start": v(709.75, 55.6) * mm, "mid": v(707.27, 46.73) * mm, "end": v(706.44, 37.56) * mm});
            skLineSegment(sketch, "E39.7.0.25", {"start": v(705.93, 81.11) * mm, "end": v(705.93, 82.56) * mm});
            skArc(sketch, "E39.7.0.26", {"start": v(705.93, 81.11) * mm, "mid": v(706.52, 78.08) * mm, "end": v(707.83, 75.27) * mm});
            skLineSegment(sketch, "E39.7.0.27", {"start": v(671.51, 82.55) * mm, "end": v(671.51, 81.1) * mm});
            skArc(sketch, "E39.7.0.28", {"start": v(669.78, 74.7) * mm, "mid": v(671.07, 77.8) * mm, "end": v(671.51, 81.1) * mm});
            skLineSegment(sketch, "E39.8.0.0", {"start": v(755.65, 311.15) * mm, "end": v(819.15, 311.15) * mm, "construction": true});
            skLineSegment(sketch, "E39.8.0.1", {"start": v(819.15, 311.15) * mm, "end": v(819.15, 114.3) * mm, "construction": true});
            skLineSegment(sketch, "E39.8.0.2", {"start": v(738.19, 114.3) * mm, "end": v(738.19, 293.69) * mm});
            skArc(sketch, "E39.8.0.3", {"start": v(836.61, 293.69) * mm, "mid": v(787.4, 342.9) * mm, "end": v(738.19, 293.69) * mm});
            skLineSegment(sketch, "E39.8.0.4", {"start": v(755.65, 114.3) * mm, "end": v(819.15, 114.3) * mm, "construction": true});
            skPoint(sketch, "E39.8.0.5", {"position": v(769.94, 49.75) * mm});
            skLineSegment(sketch, "E39.8.0.6", {"start": v(755.65, 311.15) * mm, "end": v(755.65, 114.3) * mm, "construction": true});
            skLineSegment(sketch, "E39.8.0.7", {"start": v(787.4, 342.9) * mm, "end": v(787.4, 0) * mm, "construction": true});
            skPoint(sketch, "E39.8.0.8", {"position": v(804.86, 83.6) * mm});
            skArc(sketch, "E39.8.0.9", {"start": v(738.19, 114.3) * mm, "mid": v(742.84, 103.07) * mm, "end": v(754.06, 98.43) * mm});
            skArc(sketch, "E39.8.0.10", {"start": v(820.74, 98.43) * mm, "mid": v(831.96, 103.07) * mm, "end": v(836.61, 114.3) * mm});
            skLineSegment(sketch, "E39.8.0.11", {"start": v(719.14, 37.56) * mm, "end": v(817.56, 38.71) * mm, "construction": true});
            skPoint(sketch, "E39.8.0.12", {"position": v(769.94, 77.25) * mm});
            skPoint(sketch, "E39.8.0.13", {"position": v(804.86, 49.75) * mm});
            skArc(sketch, "E39.8.0.14", {"start": v(769.94, 17.46) * mm, "mid": v(787.4, 0) * mm, "end": v(804.86, 17.46) * mm});
            skArc(sketch, "E39.8.0.15", {"start": v(769.94, 82.55) * mm, "mid": v(765.29, 93.78) * mm, "end": v(754.06, 98.43) * mm});
            skLineSegment(sketch, "E39.8.0.16", {"start": v(719.14, 37.56) * mm, "end": v(817.56, 37.56) * mm, "construction": true});
            skArc(sketch, "E39.8.0.17", {"start": v(769.94, 37.56) * mm, "mid": v(769.1, 46.73) * mm, "end": v(766.62, 55.6) * mm});
            skArc(sketch, "E39.8.0.18", {"start": v(820.74, 98.43) * mm, "mid": v(809.19, 93.96) * mm, "end": v(804.36, 82.56) * mm});
            skLineSegment(sketch, "E39.8.0.19", {"start": v(804.86, 37.56) * mm, "end": v(804.86, 17.46) * mm});
            skLineSegment(sketch, "E39.8.0.20", {"start": v(765.18, 63.5) * mm, "end": v(809.63, 63.5) * mm, "construction": true});
            skArc(sketch, "E39.8.0.21", {"start": v(768.2, 74.7) * mm, "mid": v(765.25, 65.33) * mm, "end": v(766.62, 55.6) * mm});
            skLineSegment(sketch, "E39.8.0.22", {"start": v(769.94, 37.56) * mm, "end": v(769.94, 17.46) * mm});
            skArc(sketch, "E39.8.0.23", {"start": v(808.18, 55.6) * mm, "mid": v(809.52, 65.66) * mm, "end": v(806.25, 75.27) * mm});
            skArc(sketch, "E39.8.0.24", {"start": v(808.18, 55.6) * mm, "mid": v(805.7, 46.73) * mm, "end": v(804.86, 37.56) * mm});
            skLineSegment(sketch, "E39.8.0.25", {"start": v(804.36, 81.11) * mm, "end": v(804.36, 82.56) * mm});
            skArc(sketch, "E39.8.0.26", {"start": v(804.36, 81.11) * mm, "mid": v(804.95, 78.08) * mm, "end": v(806.25, 75.27) * mm});
            skLineSegment(sketch, "E39.8.0.27", {"start": v(769.94, 82.55) * mm, "end": v(769.94, 81.1) * mm});
            skArc(sketch, "E39.8.0.28", {"start": v(768.2, 74.7) * mm, "mid": v(769.5, 77.8) * mm, "end": v(769.94, 81.1) * mm});
            skLineSegment(sketch, "E39.9.0.0", {"start": v(854.08, 311.15) * mm, "end": v(917.58, 311.15) * mm, "construction": true});
            skLineSegment(sketch, "E39.9.0.1", {"start": v(917.58, 311.15) * mm, "end": v(917.58, 114.3) * mm, "construction": true});
            skLineSegment(sketch, "E39.9.0.2", {"start": v(836.61, 114.3) * mm, "end": v(836.61, 293.69) * mm});
            skArc(sketch, "E39.9.0.3", {"start": v(935.04, 293.69) * mm, "mid": v(885.83, 342.9) * mm, "end": v(836.61, 293.69) * mm});
            skLineSegment(sketch, "E39.9.0.4", {"start": v(854.08, 114.3) * mm, "end": v(917.58, 114.3) * mm, "construction": true});
            skPoint(sketch, "E39.9.0.5", {"position": v(868.36, 49.75) * mm});
            skLineSegment(sketch, "E39.9.0.6", {"start": v(854.08, 311.15) * mm, "end": v(854.08, 114.3) * mm, "construction": true});
            skLineSegment(sketch, "E39.9.0.7", {"start": v(885.82, 342.9) * mm, "end": v(885.83, 0) * mm, "construction": true});
            skPoint(sketch, "E39.9.0.8", {"position": v(903.29, 83.6) * mm});
            skArc(sketch, "E39.9.0.9", {"start": v(836.61, 114.3) * mm, "mid": v(841.26, 103.07) * mm, "end": v(852.49, 98.43) * mm});
            skArc(sketch, "E39.9.0.10", {"start": v(919.16, 98.43) * mm, "mid": v(930.39, 103.07) * mm, "end": v(935.04, 114.3) * mm});
            skLineSegment(sketch, "E39.9.0.11", {"start": v(817.56, 37.56) * mm, "end": v(915.98, 38.71) * mm, "construction": true});
            skPoint(sketch, "E39.9.0.12", {"position": v(868.36, 77.25) * mm});
            skPoint(sketch, "E39.9.0.13", {"position": v(903.29, 49.75) * mm});
            skArc(sketch, "E39.9.0.14", {"start": v(868.36, 17.46) * mm, "mid": v(885.83, 0) * mm, "end": v(903.29, 17.46) * mm});
            skArc(sketch, "E39.9.0.15", {"start": v(868.36, 82.55) * mm, "mid": v(863.71, 93.78) * mm, "end": v(852.49, 98.43) * mm});
            skLineSegment(sketch, "E39.9.0.16", {"start": v(817.56, 37.56) * mm, "end": v(915.99, 37.56) * mm, "construction": true});
            skArc(sketch, "E39.9.0.17", {"start": v(868.36, 37.56) * mm, "mid": v(867.53, 46.73) * mm, "end": v(865.05, 55.6) * mm});
            skArc(sketch, "E39.9.0.18", {"start": v(919.16, 98.43) * mm, "mid": v(907.61, 93.96) * mm, "end": v(902.78, 82.56) * mm});
            skLineSegment(sketch, "E39.9.0.19", {"start": v(903.29, 37.56) * mm, "end": v(903.29, 17.46) * mm});
            skLineSegment(sketch, "E39.9.0.20", {"start": v(863.6, 63.5) * mm, "end": v(908.05, 63.5) * mm, "construction": true});
            skArc(sketch, "E39.9.0.21", {"start": v(866.63, 74.7) * mm, "mid": v(863.68, 65.33) * mm, "end": v(865.05, 55.6) * mm});
            skLineSegment(sketch, "E39.9.0.22", {"start": v(868.36, 37.56) * mm, "end": v(868.36, 17.46) * mm});
            skArc(sketch, "E39.9.0.23", {"start": v(906.6, 55.6) * mm, "mid": v(907.94, 65.66) * mm, "end": v(904.68, 75.27) * mm});
            skArc(sketch, "E39.9.0.24", {"start": v(906.6, 55.6) * mm, "mid": v(904.12, 46.73) * mm, "end": v(903.29, 37.56) * mm});
            skLineSegment(sketch, "E39.9.0.25", {"start": v(902.78, 81.11) * mm, "end": v(902.78, 82.56) * mm});
            skArc(sketch, "E39.9.0.26", {"start": v(902.78, 81.11) * mm, "mid": v(903.37, 78.08) * mm, "end": v(904.68, 75.27) * mm});
            skLineSegment(sketch, "E39.9.0.27", {"start": v(868.36, 82.55) * mm, "end": v(868.36, 81.1) * mm});
            skArc(sketch, "E39.9.0.28", {"start": v(866.63, 74.7) * mm, "mid": v(867.92, 77.8) * mm, "end": v(868.36, 81.1) * mm});
            skLineSegment(sketch, "E39.10.0.0", {"start": v(952.5, 311.15) * mm, "end": v(1016, 311.15) * mm, "construction": true});
            skLineSegment(sketch, "E39.10.0.1", {"start": v(1016, 311.15) * mm, "end": v(1016, 114.3) * mm, "construction": true});
            skLineSegment(sketch, "E39.10.0.2", {"start": v(935.04, 114.3) * mm, "end": v(935.04, 293.69) * mm});
            skArc(sketch, "E39.10.0.3", {"start": v(1033.46, 293.69) * mm, "mid": v(984.25, 342.9) * mm, "end": v(935.04, 293.69) * mm});
            skLineSegment(sketch, "E39.10.0.4", {"start": v(952.5, 114.3) * mm, "end": v(1016, 114.3) * mm, "construction": true});
            skPoint(sketch, "E39.10.0.5", {"position": v(966.79, 49.75) * mm});
            skLineSegment(sketch, "E39.10.0.6", {"start": v(952.5, 311.15) * mm, "end": v(952.5, 114.3) * mm, "construction": true});
            skLineSegment(sketch, "E39.10.0.7", {"start": v(984.25, 342.9) * mm, "end": v(984.25, 0) * mm, "construction": true});
            skPoint(sketch, "E39.10.0.8", {"position": v(1001.71, 83.6) * mm});
            skArc(sketch, "E39.10.0.9", {"start": v(935.04, 114.3) * mm, "mid": v(939.69, 103.07) * mm, "end": v(950.91, 98.43) * mm});
            skArc(sketch, "E39.10.0.10", {"start": v(1017.59, 98.43) * mm, "mid": v(1028.81, 103.07) * mm, "end": v(1033.46, 114.3) * mm});
            skLineSegment(sketch, "E39.10.0.11", {"start": v(915.99, 37.56) * mm, "end": v(1014.4, 38.71) * mm, "construction": true});
            skPoint(sketch, "E39.10.0.12", {"position": v(966.79, 77.25) * mm});
            skPoint(sketch, "E39.10.0.13", {"position": v(1001.71, 49.75) * mm});
            skArc(sketch, "E39.10.0.14", {"start": v(966.79, 17.46) * mm, "mid": v(984.25, 0) * mm, "end": v(1001.71, 17.46) * mm});
            skArc(sketch, "E39.10.0.15", {"start": v(966.79, 82.55) * mm, "mid": v(962.14, 93.78) * mm, "end": v(950.91, 98.43) * mm});
            skLineSegment(sketch, "E39.10.0.16", {"start": v(915.99, 37.56) * mm, "end": v(1014.41, 37.56) * mm, "construction": true});
            skArc(sketch, "E39.10.0.17", {"start": v(966.79, 37.56) * mm, "mid": v(965.95, 46.73) * mm, "end": v(963.47, 55.6) * mm});
            skArc(sketch, "E39.10.0.18", {"start": v(1017.59, 98.43) * mm, "mid": v(1006.04, 93.96) * mm, "end": v(1001.2, 82.56) * mm});
            skLineSegment(sketch, "E39.10.0.19", {"start": v(1001.71, 37.56) * mm, "end": v(1001.71, 17.46) * mm});
            skLineSegment(sketch, "E39.10.0.20", {"start": v(962.02, 63.5) * mm, "end": v(1006.48, 63.5) * mm, "construction": true});
            skArc(sketch, "E39.10.0.21", {"start": v(965.06, 74.7) * mm, "mid": v(962.1, 65.33) * mm, "end": v(963.47, 55.6) * mm});
            skLineSegment(sketch, "E39.10.0.22", {"start": v(966.79, 37.56) * mm, "end": v(966.79, 17.46) * mm});
            skArc(sketch, "E39.10.0.23", {"start": v(1005.03, 55.6) * mm, "mid": v(1006.37, 65.66) * mm, "end": v(1003.1, 75.27) * mm});
            skArc(sketch, "E39.10.0.24", {"start": v(1005.03, 55.6) * mm, "mid": v(1002.55, 46.73) * mm, "end": v(1001.71, 37.56) * mm});
            skLineSegment(sketch, "E39.10.0.25", {"start": v(1001.2, 81.11) * mm, "end": v(1001.2, 82.56) * mm});
            skArc(sketch, "E39.10.0.26", {"start": v(1001.2, 81.11) * mm, "mid": v(1001.8, 78.08) * mm, "end": v(1003.1, 75.27) * mm});
            skLineSegment(sketch, "E39.10.0.27", {"start": v(966.79, 82.55) * mm, "end": v(966.79, 81.1) * mm});
            skArc(sketch, "E39.10.0.28", {"start": v(965.06, 74.7) * mm, "mid": v(966.35, 77.8) * mm, "end": v(966.79, 81.1) * mm});
            skLineSegment(sketch, "E39.11.0.0", {"start": v(1050.93, 311.15) * mm, "end": v(1114.42, 311.15) * mm, "construction": true});
            skLineSegment(sketch, "E39.11.0.1", {"start": v(1114.42, 311.15) * mm, "end": v(1114.42, 114.3) * mm, "construction": true});
            skLineSegment(sketch, "E39.11.0.2", {"start": v(1033.46, 114.3) * mm, "end": v(1033.46, 293.69) * mm});
            skArc(sketch, "E39.11.0.3", {"start": v(1131.89, 293.69) * mm, "mid": v(1082.67, 342.9) * mm, "end": v(1033.46, 293.69) * mm});
            skLineSegment(sketch, "E39.11.0.4", {"start": v(1050.92, 114.3) * mm, "end": v(1114.43, 114.3) * mm, "construction": true});
            skPoint(sketch, "E39.11.0.5", {"position": v(1065.21, 49.75) * mm});
            skLineSegment(sketch, "E39.11.0.6", {"start": v(1050.93, 311.15) * mm, "end": v(1050.93, 114.3) * mm, "construction": true});
            skLineSegment(sketch, "E39.11.0.7", {"start": v(1082.67, 342.9) * mm, "end": v(1082.67, 0) * mm, "construction": true});
            skPoint(sketch, "E39.11.0.8", {"position": v(1100.14, 83.6) * mm});
            skArc(sketch, "E39.11.0.9", {"start": v(1033.46, 114.3) * mm, "mid": v(1038.11, 103.07) * mm, "end": v(1049.34, 98.43) * mm});
            skArc(sketch, "E39.11.0.10", {"start": v(1116.01, 98.43) * mm, "mid": v(1127.24, 103.07) * mm, "end": v(1131.89, 114.3) * mm});
            skLineSegment(sketch, "E39.11.0.11", {"start": v(1014.41, 37.56) * mm, "end": v(1112.83, 38.71) * mm, "construction": true});
            skPoint(sketch, "E39.11.0.12", {"position": v(1065.21, 77.25) * mm});
            skPoint(sketch, "E39.11.0.13", {"position": v(1100.14, 49.75) * mm});
            skArc(sketch, "E39.11.0.14", {"start": v(1065.21, 17.46) * mm, "mid": v(1082.67, 0) * mm, "end": v(1100.14, 17.46) * mm});
            skArc(sketch, "E39.11.0.15", {"start": v(1065.21, 82.55) * mm, "mid": v(1060.56, 93.78) * mm, "end": v(1049.34, 98.43) * mm});
            skLineSegment(sketch, "E39.11.0.16", {"start": v(1014.41, 37.56) * mm, "end": v(1112.84, 37.56) * mm, "construction": true});
            skArc(sketch, "E39.11.0.17", {"start": v(1065.21, 37.56) * mm, "mid": v(1064.38, 46.73) * mm, "end": v(1061.9, 55.6) * mm});
            skArc(sketch, "E39.11.0.18", {"start": v(1116.01, 98.43) * mm, "mid": v(1104.46, 93.96) * mm, "end": v(1099.63, 82.56) * mm});
            skLineSegment(sketch, "E39.11.0.19", {"start": v(1100.14, 37.56) * mm, "end": v(1100.14, 17.46) * mm});
            skLineSegment(sketch, "E39.11.0.20", {"start": v(1060.45, 63.5) * mm, "end": v(1104.9, 63.5) * mm, "construction": true});
            skArc(sketch, "E39.11.0.21", {"start": v(1063.48, 74.7) * mm, "mid": v(1060.53, 65.33) * mm, "end": v(1061.9, 55.6) * mm});
            skLineSegment(sketch, "E39.11.0.22", {"start": v(1065.21, 37.56) * mm, "end": v(1065.21, 17.46) * mm});
            skArc(sketch, "E39.11.0.23", {"start": v(1103.45, 55.6) * mm, "mid": v(1104.8, 65.66) * mm, "end": v(1101.53, 75.27) * mm});
            skArc(sketch, "E39.11.0.24", {"start": v(1103.45, 55.6) * mm, "mid": v(1100.97, 46.73) * mm, "end": v(1100.14, 37.56) * mm});
            skLineSegment(sketch, "E39.11.0.25", {"start": v(1099.63, 81.11) * mm, "end": v(1099.63, 82.56) * mm});
            skArc(sketch, "E39.11.0.26", {"start": v(1099.63, 81.11) * mm, "mid": v(1100.22, 78.08) * mm, "end": v(1101.53, 75.27) * mm});
            skLineSegment(sketch, "E39.11.0.27", {"start": v(1065.21, 82.55) * mm, "end": v(1065.21, 81.1) * mm});
            skArc(sketch, "E39.11.0.28", {"start": v(1063.48, 74.7) * mm, "mid": v(1064.77, 77.8) * mm, "end": v(1065.21, 81.1) * mm});
            skText(sketch, "E40", { "text": "W", "fontName": "RobotoSlab-Bold.ttf"});
            skText(sketch, "E41", { "text": "W", "fontName": "RobotoSlab-Bold.ttf"});
            skText(sketch, "E42", { "text": "W", "fontName": "RobotoSlab-Bold.ttf"});
            skText(sketch, "E43", { "text": "W", "fontName": "RobotoSlab-Bold.ttf"});
            skText(sketch, "E44", { "text": "W", "fontName": "RobotoSlab-Bold.ttf"});
            skText(sketch, "E45", { "text": "W", "fontName": "RobotoSlab-Bold.ttf"});
            skText(sketch, "E46", { "text": "W", "fontName": "RobotoSlab-Bold.ttf"});
            skText(sketch, "E47", { "text": "W", "fontName": "RobotoSlab-Bold.ttf"});
            skText(sketch, "E48", { "text": "W", "fontName": "RobotoSlab-Bold.ttf"});
            skText(sketch, "E49", { "text": "W", "fontName": "RobotoSlab-Bold.ttf"});
            skText(sketch, "E50", { "text": "W", "fontName": "RobotoSlab-Bold.ttf"});
            skLineSegment(sketch, "E51", {"start": v(1131.89, 293.69) * mm, "end": v(1131.89, 114.3) * mm});
            const initialGuessF1  = {"E35": [-0.01183, 0.0546, 1, 0, 0.01778], "E40": [0.0866, 0.05461, 1, 0, 0.01778], "E41": [0.18502, 0.05461, 1, 0, 0.01778], "E42": [0.28345, 0.05461, 1, 0, 0.01778], "E43": [0.38187, 0.05461, 1, 0, 0.01778], "E44": [0.4803, 0.05461, 1, 0, 0.01778], "E45": [0.57872, 0.05461, 1, 0, 0.01778], "E46": [0.67715, 0.05461, 1, 0, 0.01778], "E47": [0.77557, 0.05461, 1, 0, 0.01778], "E48": [0.874, 0.05461, 1, 0, 0.01778], "E49": [0.97242, 0.05461, 1, 0, 0.01778], "E50": [1.07085, 0.05461, 1, 0, 0.01778]};
            skSetInitialGuess(sketch, initialGuessF1);
            skSolve(sketch);
        }
        {
            var Q0;
            Q0=makeQuery(id+"F1.imprint","IMPRINT",FACE,{"disambiguationData":[TD([[makeQuery(id+"F1.imprint","IMPRINT",EDGE,{"derivedFrom":sQuery(id+"F1.wireOp",EDGE,"E15.left")}),-1.0]])]});
            extrude(context, id + "F2", {"entities" : qUnion([Q0]), "depth" : 12.7 * mm, "offsetDistance" : 25.4 * mm});
        }
    });
